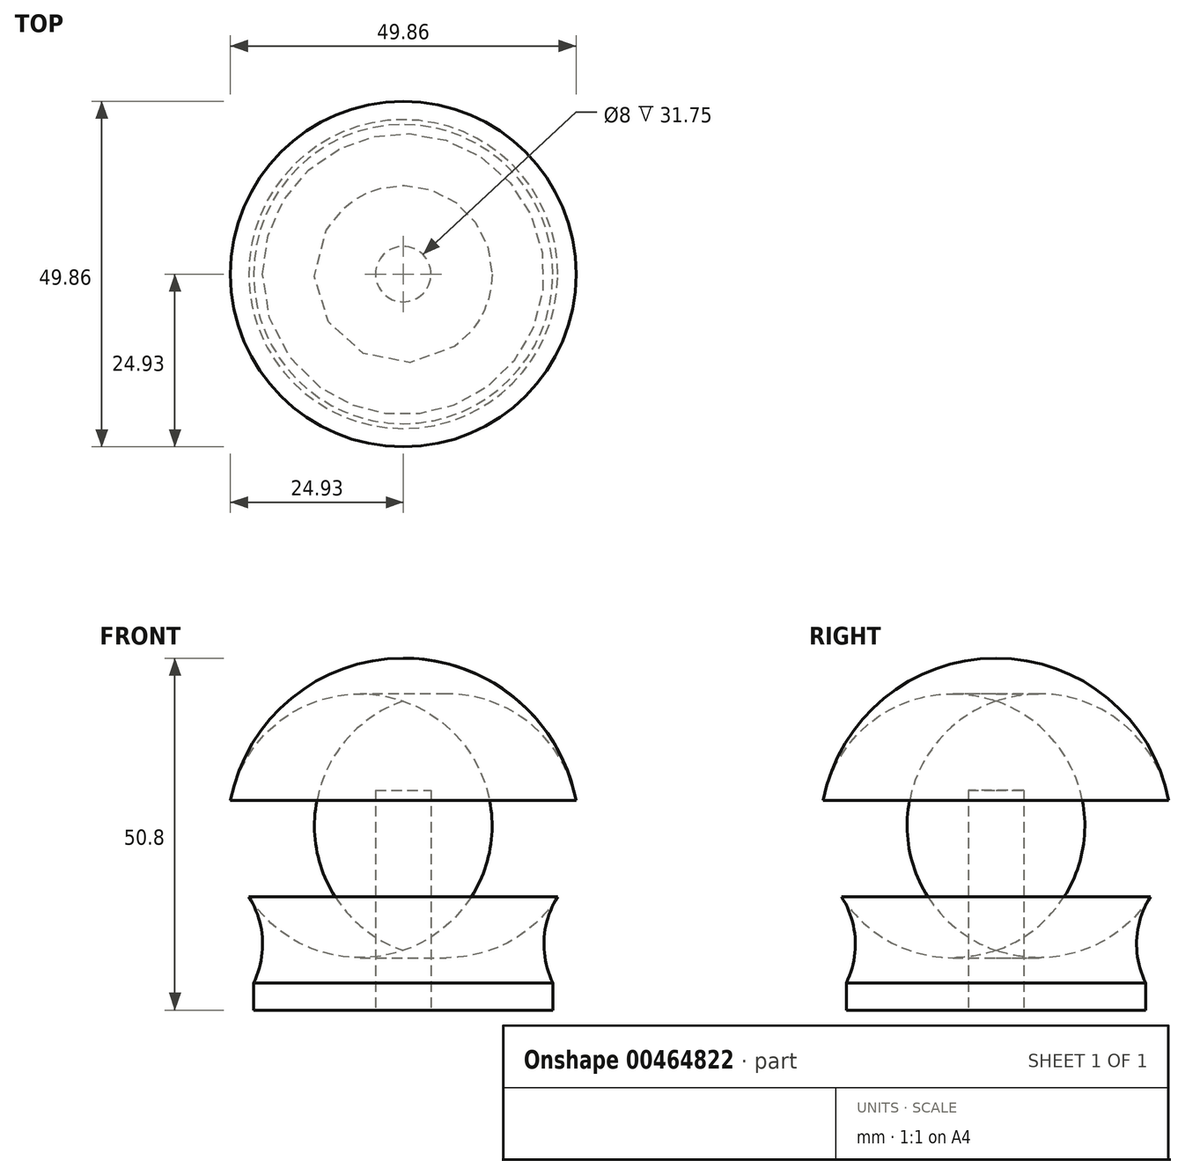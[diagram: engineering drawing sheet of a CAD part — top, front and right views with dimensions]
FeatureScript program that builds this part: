
annotation { "Feature Type Name" : "Feature", "Feature Type Description" : "" }
export const myFeature = defineFeature(function(context is Context, id is Id, definition is map)
    precondition{}
    {
        {
            var Q0;
            Q0=qCreatedBy(makeId("Front.planeOp"),FACE);
            var sketch = newSketch(context, id + "F0", { "sketchPlane" : qUnion([Q0])});
            skArc(sketch, "E0", {"start": v(24.6, 19.05) * mm, "mid": v(20.54, 12) * mm, "end": v(21.6, 3.94) * mm});
            skLineSegment(sketch, "E1", {"start": v(21.59, 0) * mm, "end": v(0, 0) * mm});
            skArc(sketch, "E2", {"start": v(24.6, 19.05) * mm, "mid": v(20.08, 40.95) * mm, "end": v(0, 50.8) * mm});
            skLineSegment(sketch, "E3", {"start": v(21.59, 3.94) * mm, "end": v(21.59, 0) * mm});
            skPoint(sketch, "E4.orphan", {"position": v(24.6, 0) * mm});
            skLineSegment(sketch, "E5", {"start": v(0, 31.75) * mm, "end": v(4, 31.75) * mm});
            skLineSegment(sketch, "E6", {"start": v(4, 31.75) * mm, "end": v(4, 0) * mm});
            skLineSegment(sketch, "E7.trimOffspring", {"start": v(0, 31.75) * mm, "end": v(0, 50.8) * mm});
            skSolve(sketch);
        }
        {
            var Q0;
            Q0 = qSketchRegion(id + "F0", true);
            var Q1;
            Q1=sQuery(id+"F0.wireOp",EDGE,"E7.trimOffspring");
            revolve(context, id + "F1", {"surfaceOperationType" : NewSurfaceOperationType.NEW, "entities" : qUnion([Q0]), "axis" : qUnion([Q1]), "revolveType" : RevolveType.FULL});
        }
        {
            var Q0;
            Q0=makeQuery(id+"F1.opRevolve","SWEPT_EDGE",EDGE,{"disambiguationData":[OSD([sQuery(id+"F0.wireOp",EDGE,"E0"),sQuery(id+"F0.wireOp",EDGE,"E2")])]});
            fillet(context, id + "F2", {"entities" : qUnion([Q0]), "radius" : 19.05 * mm, "tangentPropagation" : true, "allowEdgeOverflow" : false});
        }
    });
